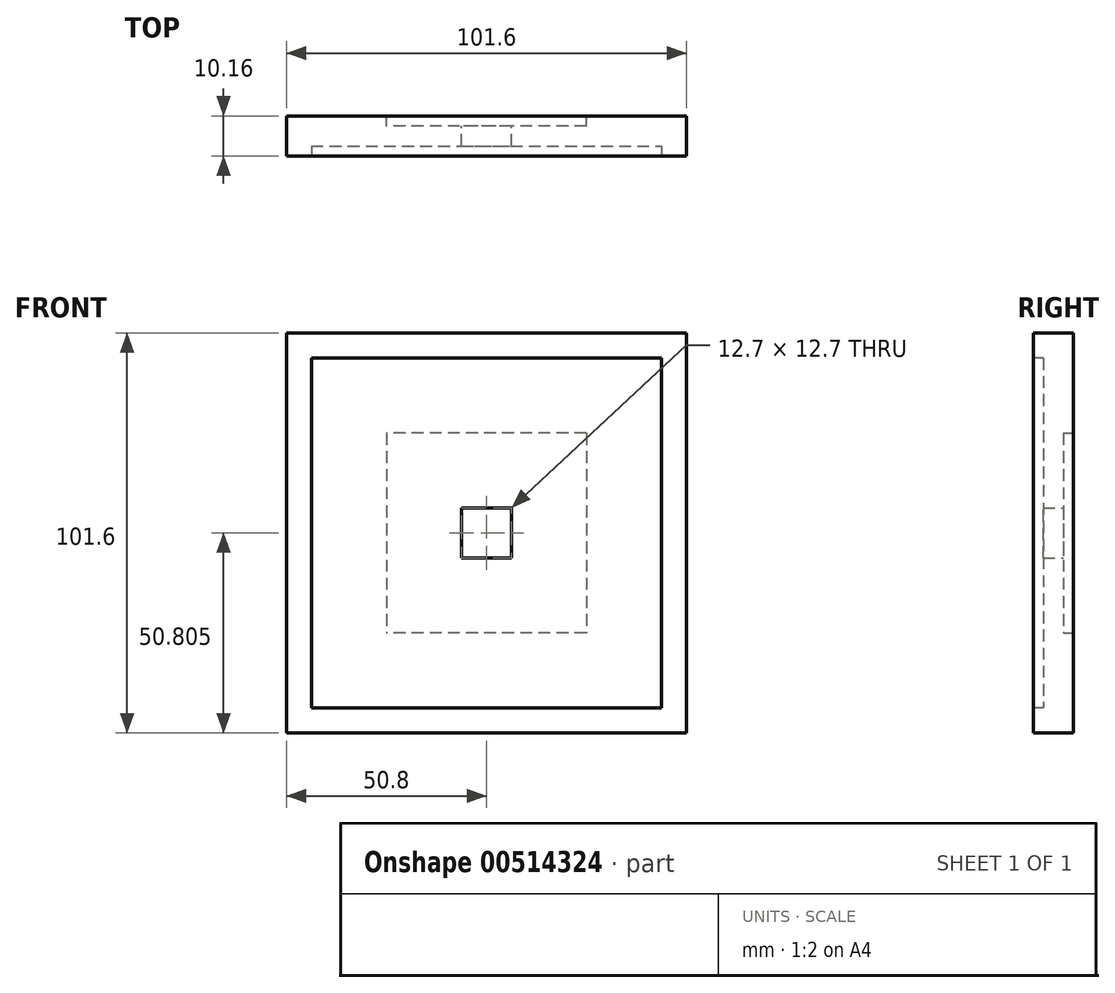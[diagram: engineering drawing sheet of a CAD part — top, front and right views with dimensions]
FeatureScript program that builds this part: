
annotation { "Feature Type Name" : "Feature", "Feature Type Description" : "" }
export const myFeature = defineFeature(function(context is Context, id is Id, definition is map)
    precondition{}
    {
        {
            var Q0;
            Q0=qCreatedBy(makeId("Front.planeOp"),FACE);
            var sketch = newSketch(context, id + "F0", { "sketchPlane" : qUnion([Q0])});
            skLineSegment(sketch, "E0.bottom", {"start": v(-46.73, 56.81) * mm, "end": v(54.87, 56.81) * mm});
            skLineSegment(sketch, "E0.top", {"start": v(-46.73, -44.79) * mm, "end": v(54.87, -44.79) * mm});
            skLineSegment(sketch, "E0.left", {"start": v(-46.73, 56.81) * mm, "end": v(-46.73, -44.79) * mm});
            skLineSegment(sketch, "E0.right", {"start": v(54.87, 56.81) * mm, "end": v(54.87, -44.79) * mm});
            skSolve(sketch);
        }
        {
            var Q0;
            Q0=makeQuery(id+"F0.imprint","IMPRINT",FACE,{"disambiguationData":[TD([[makeQuery(id+"F0.imprint","IMPRINT",EDGE,{"derivedFrom":sQuery(id+"F0.wireOp",EDGE,"E0.bottom")}),-1.0]])]});
            extrude(context, id + "F1", {"entities" : qUnion([Q0]), "depth" : 10.16 * mm});
        }
        {
            var Q0;
            Q0=makeQuery(id+"F1.opExtrude","CAP_FACE",FACE,{"disambiguationData":[OSD([sQuery(id+"F0.wireOp",EDGE,"E0.bottom"),sQuery(id+"F0.wireOp",EDGE,"E0.top"),sQuery(id+"F0.wireOp",EDGE,"E0.left"),sQuery(id+"F0.wireOp",EDGE,"E0.right")])],"isStart":false});
            var sketch = newSketch(context, id + "F2", { "sketchPlane" : qUnion([Q0])});
            skLineSegment(sketch, "E1.bottom", {"start": v(-40.38, 50.46) * mm, "end": v(48.52, 50.46) * mm});
            skLineSegment(sketch, "E1.top", {"start": v(-40.38, -38.44) * mm, "end": v(48.52, -38.44) * mm});
            skLineSegment(sketch, "E1.left", {"start": v(-40.38, 50.46) * mm, "end": v(-40.38, -38.44) * mm});
            skLineSegment(sketch, "E1.right", {"start": v(48.52, 50.46) * mm, "end": v(48.52, -38.44) * mm});
            skSolve(sketch);
        }
        {
            var Q0;
            Q0=makeQuery(id+"F2.imprint","IMPRINT",FACE,{"disambiguationData":[TD([[makeQuery(id+"F2.imprint","IMPRINT",EDGE,{"derivedFrom":sQuery(id+"F2.wireOp",EDGE,"E1.bottom")}),-1.0]])]});
            extrude(context, id + "F3", {"entities" : qUnion([Q0]), "operationType" : NewBodyOperationType.REMOVE, "oppositeDirection" : true, "depth" : 2.54 * mm});
        }
        {
            var Q0;
            Q0=makeQuery(id+"F1.opExtrude","CAP_FACE",FACE,{"disambiguationData":[OSD([sQuery(id+"F0.wireOp",EDGE,"E0.bottom"),sQuery(id+"F0.wireOp",EDGE,"E0.top"),sQuery(id+"F0.wireOp",EDGE,"E0.left"),sQuery(id+"F0.wireOp",EDGE,"E0.right")])],"isStart":true});
            var sketch = newSketch(context, id + "F4", { "sketchPlane" : qUnion([Q0])});
            skLineSegment(sketch, "E2.bottom", {"start": v(-29.47, 31.41) * mm, "end": v(21.33, 31.41) * mm});
            skLineSegment(sketch, "E2.top", {"start": v(-29.47, -19.39) * mm, "end": v(21.33, -19.39) * mm});
            skLineSegment(sketch, "E2.left", {"start": v(-29.47, 31.41) * mm, "end": v(-29.47, -19.39) * mm});
            skLineSegment(sketch, "E2.right", {"start": v(21.33, 31.41) * mm, "end": v(21.33, -19.39) * mm});
            skSolve(sketch);
        }
        {
            var Q0;
            Q0=makeQuery(id+"F4.imprint","IMPRINT",FACE,{"disambiguationData":[TD([[makeQuery(id+"F4.imprint","IMPRINT",EDGE,{"derivedFrom":sQuery(id+"F4.wireOp",EDGE,"E2.bottom")}),-1.0]])]});
            extrude(context, id + "F5", {"entities" : qUnion([Q0]), "operationType" : NewBodyOperationType.REMOVE, "oppositeDirection" : true, "depth" : 2.54 * mm});
        }
        {
            var Q0;
            Q0=makeQuery(id+"F5.boolean.opBoolean","COPY",FACE,{"derivedFrom":makeQuery(id+"F5.opExtrude","CAP_FACE",FACE,{"disambiguationData":[OSD([sQuery(id+"F4.wireOp",EDGE,"E2.bottom"),sQuery(id+"F4.wireOp",EDGE,"E2.top"),sQuery(id+"F4.wireOp",EDGE,"E2.left"),sQuery(id+"F4.wireOp",EDGE,"E2.right")])],"isStart":false})});
            var sketch = newSketch(context, id + "F6", { "sketchPlane" : qUnion([Q0])});
            skLineSegment(sketch, "E3.bottom", {"start": v(-10.42, 12.36) * mm, "end": v(2.28, 12.36) * mm});
            skLineSegment(sketch, "E3.top", {"start": v(-10.42, -0.34) * mm, "end": v(2.28, -0.34) * mm});
            skLineSegment(sketch, "E3.left", {"start": v(-10.42, 12.36) * mm, "end": v(-10.42, -0.34) * mm});
            skLineSegment(sketch, "E3.right", {"start": v(2.28, 12.36) * mm, "end": v(2.28, -0.34) * mm});
            skSolve(sketch);
        }
        {
            var Q0;
            Q0=makeQuery(id+"F6.imprint","IMPRINT",FACE,{"disambiguationData":[TD([[makeQuery(id+"F6.imprint","IMPRINT",EDGE,{"derivedFrom":sQuery(id+"F6.wireOp",EDGE,"E3.bottom")}),-1.0]])]});
            extrude(context, id + "F7", {"entities" : qUnion([Q0]), "operationType" : NewBodyOperationType.REMOVE, "oppositeDirection" : true, "depth" : 25.4 * mm});
        }
    });
